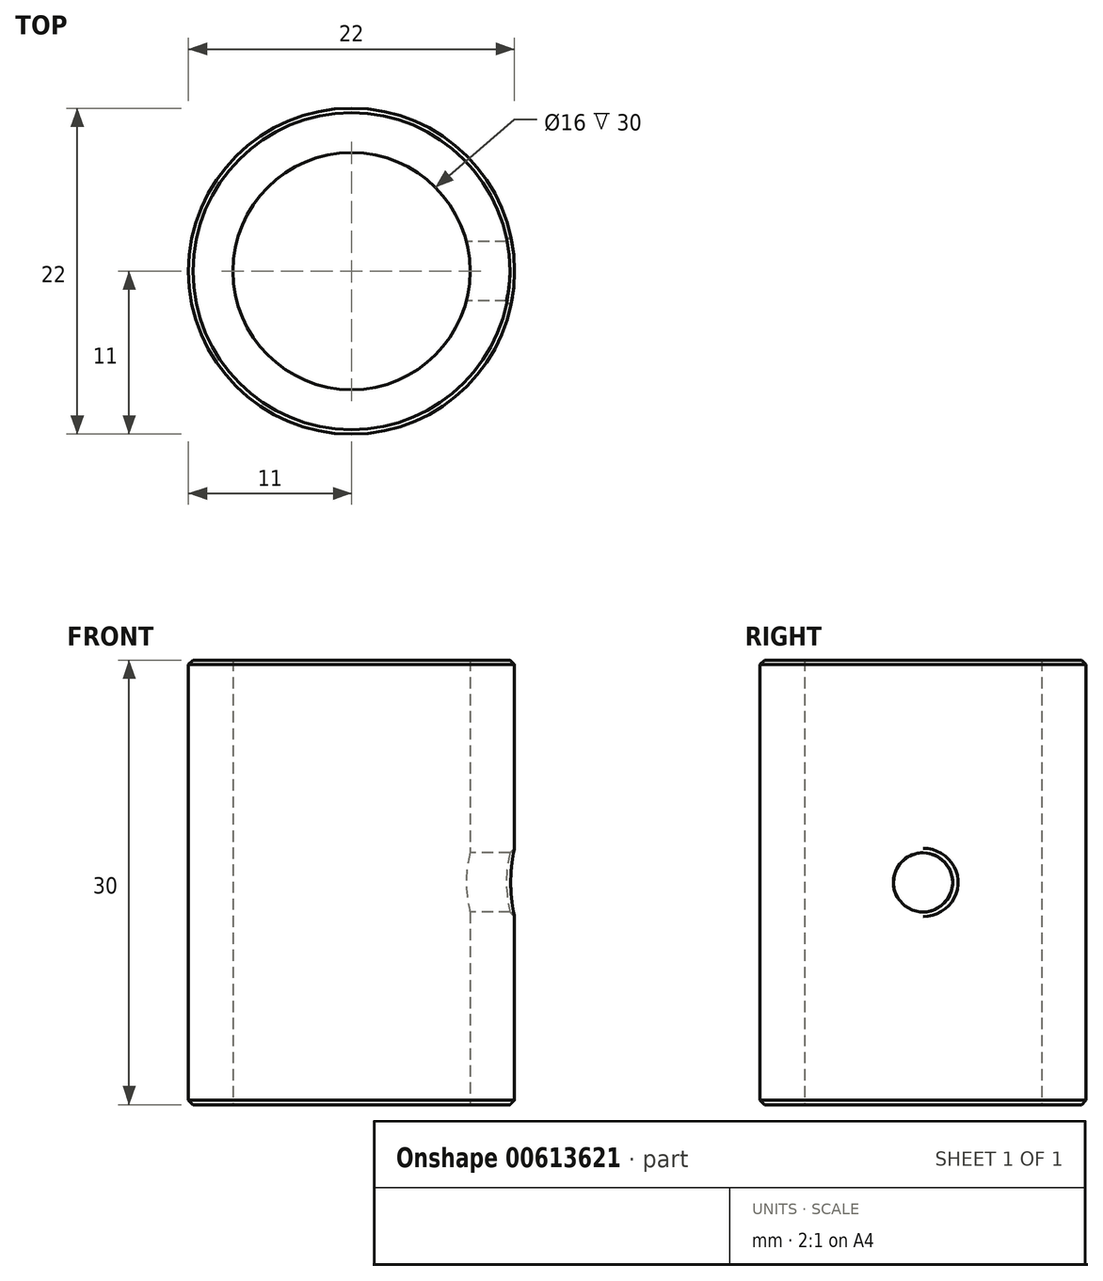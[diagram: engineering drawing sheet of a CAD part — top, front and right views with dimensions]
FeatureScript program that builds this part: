
annotation { "Feature Type Name" : "Feature", "Feature Type Description" : "" }
export const myFeature = defineFeature(function(context is Context, id is Id, definition is map)
    precondition{}
    {
        {
            var Q0;
            Q0=qCreatedBy(makeId("Top.planeOp"),FACE);
            var sketch = newSketch(context, id + "F0", { "sketchPlane" : qUnion([Q0])});
            skCircle(sketch, "E0", {"center": v(0, 0) * mm, "radius": 8 * mm});
            skCircle(sketch, "E1", {"center": v(0, 0) * mm, "radius": 11 * mm});
            skSolve(sketch);
        }
        {
            var Q0;
            Q0=qSketchRegion(id+"F0",true);
            extrude(context, id + "F1", {"entities" : qUnion([Q0]), "depth" : 15 * mm, "offsetDistance" : 25 * mm, "hasSecondDirection" : true, "secondDirectionOppositeDirection" : true, "secondDirectionDepth" : 15 * mm});
        }
        {
            var Q0;
            Q0=qCreatedBy(makeId("Right.planeOp"),FACE);
            var sketch = newSketch(context, id + "F2", { "sketchPlane" : qUnion([Q0])});
            skCircle(sketch, "E2", {"center": v(0, 0) * mm, "radius": 2 * mm});
            skCircle(sketch, "E3", {"center": v(0, 0) * mm, "radius": 3 * mm});
            skSolve(sketch);
        }
        {
            var Q0;
            Q0=qCreatedBy(makeId("Right.planeOp"),FACE);
            cPlane(context, id + "F3", {"entities" : qUnion([Q0]), "cplaneType" : CPlaneType.OFFSET, "offset" : 8 * mm, "width" : 150 * mm, "height" : 150 * mm});
        }
        {
            var Q0;
            Q0=qCreatedBy(id+"F3.planeOp",FACE);
            var sketch = newSketch(context, id + "F4", { "sketchPlane" : qUnion([Q0])});
            skCircle(sketch, "E4.0", {"center": v(0, 0) * mm, "radius": 2 * mm});
            skCircle(sketch, "E5.0", {"center": v(0, 0) * mm, "radius": 3 * mm});
            skSolve(sketch);
        }
        {
            var Q0;
            Q0=sQuery(id+"F2.wireOp",VERTEX,"E3.center");
            var Q1;
            Q1=makeQuery(id+"F1.opExtrude","SWEPT_BODY",BODY,{"disambiguationData":[OSD([sQuery(id+"F0.wireOp",EDGE,"E0"),sQuery(id+"F0.wireOp",EDGE,"E1")])]});
            hole(context, id + "F5", {"style" : HoleStyle.SIMPLE, "endStyle" : HoleEndStyle.THROUGH, "oppositeDirection" : true, "holeDiameter" : 4 * mm, "majorDiameter" : 5 * mm, "isTappedThrough" : true, "tappedDepth" : 12 * mm, "tapClearance" : 3, "locations" : qUnion([Q0]), "scope" : qUnion([Q1])});
        }
        {
            var Q0;
            Q0=makeQuery(id+"F1.opExtrude","SWEPT_FACE",FACE,{"disambiguationData":[OSD([sQuery(id+"F0.wireOp",EDGE,"E1")])]});
            chamfer(context, id + "F6", {"entities" : qUnion([Q0]), "width" : 0.3 * mm, "tangentPropagation" : true});
        }
    });
